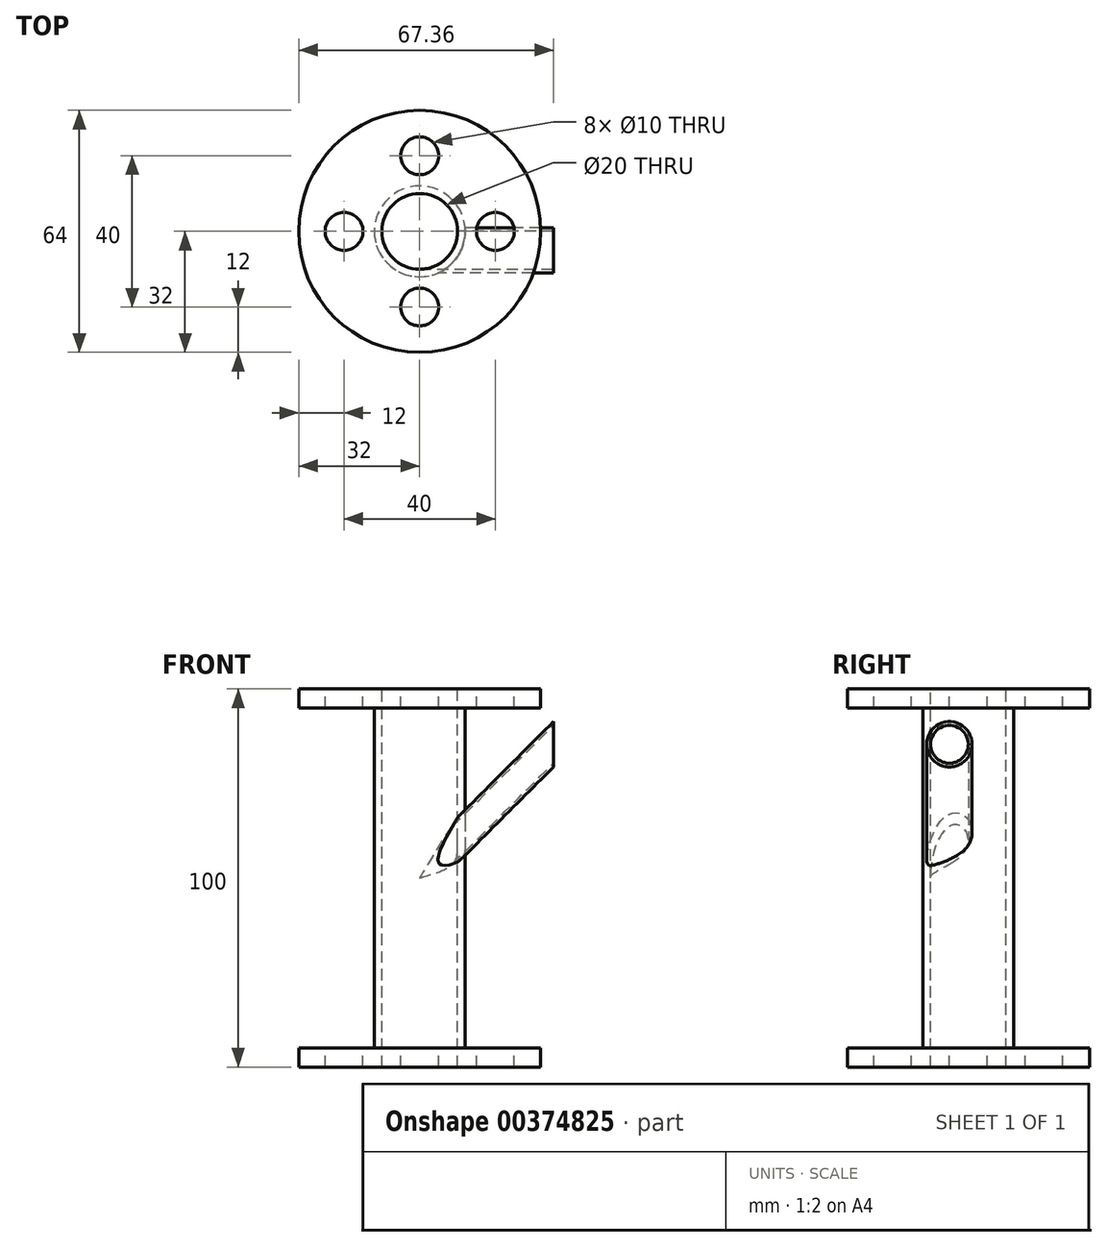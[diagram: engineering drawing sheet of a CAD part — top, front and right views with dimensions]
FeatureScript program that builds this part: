
annotation { "Feature Type Name" : "Feature", "Feature Type Description" : "" }
export const myFeature = defineFeature(function(context is Context, id is Id, definition is map)
    precondition{}
    {
        {
            var Q0;
            Q0=qCreatedBy(makeId("Top.planeOp"),FACE);
            var sketch = newSketch(context, id + "F0", { "sketchPlane" : qUnion([Q0])});
            skCircle(sketch, "E0", {"center": v(0, 0) * mm, "radius": 12 * mm});
            skSolve(sketch);
        }
        {
            var Q0;
            Q0=qSketchRegion(id+"F0",true);
            extrude(context, id + "F1", {"entities" : qUnion([Q0]), "depth" : 100 * mm, "offsetDistance" : 25 * mm});
        }
        {
            var Q0;
            Q0=makeQuery(id+"F1.opExtrude","CAP_FACE",FACE,{"disambiguationData":[OSD([sQuery(id+"F0.wireOp",EDGE,"E0")])],"isStart":false});
            var sketch = newSketch(context, id + "F2", { "sketchPlane" : qUnion([Q0])});
            skCircle(sketch, "E1", {"center": v(0, 0) * mm, "radius": 10 * mm});
            skSolve(sketch);
        }
        {
            var Q0;
            Q0=makeQuery(id+"F2.imprint","IMPRINT",FACE,{"disambiguationData":[TD([[makeQuery(id+"F2.imprint","IMPRINT",EDGE,{"derivedFrom":sQuery(id+"F2.wireOp",EDGE,"E1")}),1.0]])]});
            var Q1;
            Q1=makeQuery(id+"F1.opExtrude","CAP_FACE",FACE,{"disambiguationData":[OSD([sQuery(id+"F0.wireOp",EDGE,"E0")])],"isStart":true});
            extrude(context, id + "F3", {"entities" : qUnion([Q0]), "operationType" : NewBodyOperationType.REMOVE, "endBound" : BoundingType.UP_TO_SURFACE, "oppositeDirection" : true, "depth" : 25 * mm, "endBoundEntityFace" : qUnion([Q1]), "offsetDistance" : 25 * mm});
        }
        {
            var Q0;
            Q0=makeQuery(id+"F1.opExtrude","CAP_FACE",FACE,{"disambiguationData":[OSD([sQuery(id+"F0.wireOp",EDGE,"E0")])],"isStart":true});
            var sketch = newSketch(context, id + "F4", { "sketchPlane" : qUnion([Q0])});
            skCircle(sketch, "E2", {"center": v(0, 0) * mm, "radius": 32 * mm});
            skSolve(sketch);
        }
        {
            var Q0;
            Q0=makeQuery(id+"F4.imprint","IMPRINT",FACE,{"disambiguationData":[TD([[makeQuery(id+"F4.imprint","IMPRINT",EDGE,{"derivedFrom":sQuery(id+"F4.wireOp",EDGE,"E2")}),1.0]])]});
            extrude(context, id + "F5", {"entities" : qUnion([Q0]), "operationType" : NewBodyOperationType.ADD, "oppositeDirection" : true, "depth" : 5 * mm, "offsetDistance" : 25 * mm});
        }
        {
            var Q0;
            Q0=makeQuery(id+"F1.opExtrude","CAP_FACE",FACE,{"disambiguationData":[OSD([sQuery(id+"F0.wireOp",EDGE,"E0")])],"isStart":false});
            var sketch = newSketch(context, id + "F6", { "sketchPlane" : qUnion([Q0])});
            skCircle(sketch, "E3", {"center": v(0, 0) * mm, "radius": 32 * mm});
            skSolve(sketch);
        }
        {
            var Q0;
            Q0=makeQuery(id+"F6.imprint","IMPRINT",FACE,{"disambiguationData":[TD([[makeQuery(id+"F6.imprint","IMPRINT",EDGE,{"derivedFrom":sQuery(id+"F6.wireOp",EDGE,"E3")}),1.0]])]});
            extrude(context, id + "F7", {"entities" : qUnion([Q0]), "operationType" : NewBodyOperationType.ADD, "oppositeDirection" : true, "depth" : 5 * mm, "offsetDistance" : 25 * mm});
        }
        {
            var Q0;
            {var subQ0=sQuery(id+"F0.wireOp",EDGE,"E0");Q0=makeQuery(id+"F7.boolean.opBoolean","MERGE",FACE,{"derivedFrom":[makeQuery(id+"F1.opExtrude","CAP_FACE",FACE,{"disambiguationData":[OSD([subQ0])],"isStart":false}),makeQuery(id+"F7.opExtrude","CAP_FACE",FACE,{"disambiguationData":[OSD([subQ0,sQuery(id+"F6.wireOp",EDGE,"E3")])],"isStart":true})]});}
            var sketch = newSketch(context, id + "F8", { "sketchPlane" : qUnion([Q0])});
            skCircle(sketch, "E4", {"center": v(0, 20) * mm, "radius": 5 * mm});
            skCircle(sketch, "E5.1.0", {"center": v(-20, 0) * mm, "radius": 5 * mm});
            skCircle(sketch, "E5.2.0", {"center": v(0, -20) * mm, "radius": 5 * mm});
            skCircle(sketch, "E5.3.0", {"center": v(20, 0) * mm, "radius": 5 * mm});
            skPoint(sketch, "E5.center", {"position": v(0, 0) * mm});
            skSolve(sketch);
        }
        {
            var Q0;
            Q0=qSketchRegion(id+"F8",true);
            var Q1;
            {var subQ0=sQuery(id+"F0.wireOp",EDGE,"E0");Q1=makeQuery(id+"F5.boolean.opBoolean","MERGE",FACE,{"derivedFrom":[makeQuery(id+"F1.opExtrude","CAP_FACE",FACE,{"disambiguationData":[OSD([subQ0])],"isStart":true}),makeQuery(id+"F5.opExtrude","CAP_FACE",FACE,{"disambiguationData":[OSD([subQ0,sQuery(id+"F4.wireOp",EDGE,"E2")])],"isStart":true})]});}
            extrude(context, id + "F9", {"entities" : qUnion([Q0]), "operationType" : NewBodyOperationType.REMOVE, "endBound" : BoundingType.UP_TO_SURFACE, "oppositeDirection" : true, "depth" : 25 * mm, "endBoundEntityFace" : qUnion([Q1]), "offsetDistance" : 25 * mm});
        }
        {
            var Q0;
            Q0=qCreatedBy(makeId("Right.planeOp"),FACE);
            var sketch = newSketch(context, id + "F10", { "sketchPlane" : qUnion([Q0])});
            skLineSegment(sketch, "E6", {"start": v(0, 0) * mm, "end": v(0, 50) * mm});
            skLineSegment(sketch, "E7", {"start": v(0, 50) * mm, "end": v(-5, 50) * mm});
            skCircle(sketch, "E8", {"center": v(-5, 50) * mm, "radius": 6 * mm});
            skSolve(sketch);
        }
        {
            var Q0;
            Q0=qCreatedBy(makeId("Front.planeOp"),FACE);
            cPlane(context, id + "F11", {"entities" : qUnion([Q0]), "cplaneType" : CPlaneType.OFFSET, "offset" : 5 * mm, "width" : 150 * mm, "height" : 150 * mm});
        }
        {
            var Q0;
            Q0=qCreatedBy(id+"F11.planeOp",FACE);
            var sketch = newSketch(context, id + "F12", { "sketchPlane" : qUnion([Q0])});
            skLineSegment(sketch, "E9", {"start": v(0, 50) * mm, "end": v(35.36, 85.36) * mm});
            skSolve(sketch);
        }
        {
            var Q0;
            Q0=makeQuery(id+"F10.imprint","IMPRINT",FACE,{"disambiguationData":[TD([[makeQuery(id+"F10.imprint","IMPRINT",EDGE,{"derivedFrom":sQuery(id+"F10.wireOp",EDGE,"E8")}),1.0]])]});
            var Q1;
            Q1=sQuery(id+"F12.wireOp",EDGE,"E9");
            sweep(context, id + "F13", {"operationType" : NewBodyOperationType.ADD, "profiles" : qUnion([Q0]), "path" : qUnion([Q1])});
        }
        {
            var Q0;
            Q0=makeQuery(id+"F13.opSweep","CAP_FACE",FACE,{"disambiguationData":[OSD([sQuery(id+"F10.wireOp",EDGE,"E8"),sQuery(id+"F12.wireOp",VERTEX,"E9.end")])],"isStart":false});
            var sketch = newSketch(context, id + "F14", { "sketchPlane" : qUnion([Q0])});
            skCircle(sketch, "E10", {"center": v(-5, 85.36) * mm, "radius": 5 * mm});
            skSolve(sketch);
        }
        {
            var Q0;
            Q0=makeQuery(id+"F14.imprint","IMPRINT",FACE,{"disambiguationData":[TD([[makeQuery(id+"F14.imprint","IMPRINT",EDGE,{"derivedFrom":sQuery(id+"F14.wireOp",EDGE,"E10")}),1.0]])]});
            var Q1;
            Q1 = qConstructionFilter(qBodyType(qCreatedBy(id + "F12" ,EDGE), BodyType.WIRE), ConstructionObject.NO);
            sweep(context, id + "F15", {"operationType" : NewBodyOperationType.REMOVE, "profiles" : qUnion([Q0]), "path" : qUnion([Q1])});
        }
        {
            var Q0;
            {var subQ0=sQuery(id+"F0.wireOp",EDGE,"E0");Q0=makeQuery(id+"F7.boolean.opBoolean","MERGE",FACE,{"derivedFrom":[makeQuery(id+"F1.opExtrude","CAP_FACE",FACE,{"disambiguationData":[OSD([subQ0])],"isStart":false}),makeQuery(id+"F7.opExtrude","CAP_FACE",FACE,{"disambiguationData":[OSD([subQ0,sQuery(id+"F6.wireOp",EDGE,"E3")])],"isStart":true})]});}
            var sketch = newSketch(context, id + "F16", { "sketchPlane" : qUnion([Q0])});
            skCircle(sketch, "E11", {"center": v(0, 0) * mm, "radius": 10 * mm});
            skSolve(sketch);
        }
        {
            var Q0;
            Q0 = qSketchRegion(id + "F16", true);
            extrude(context, id + "F17", {"entities" : qUnion([Q0]), "operationType" : NewBodyOperationType.REMOVE, "oppositeDirection" : true, "depth" : 100 * mm, "offsetDistance" : 25 * mm});
        }
    });
